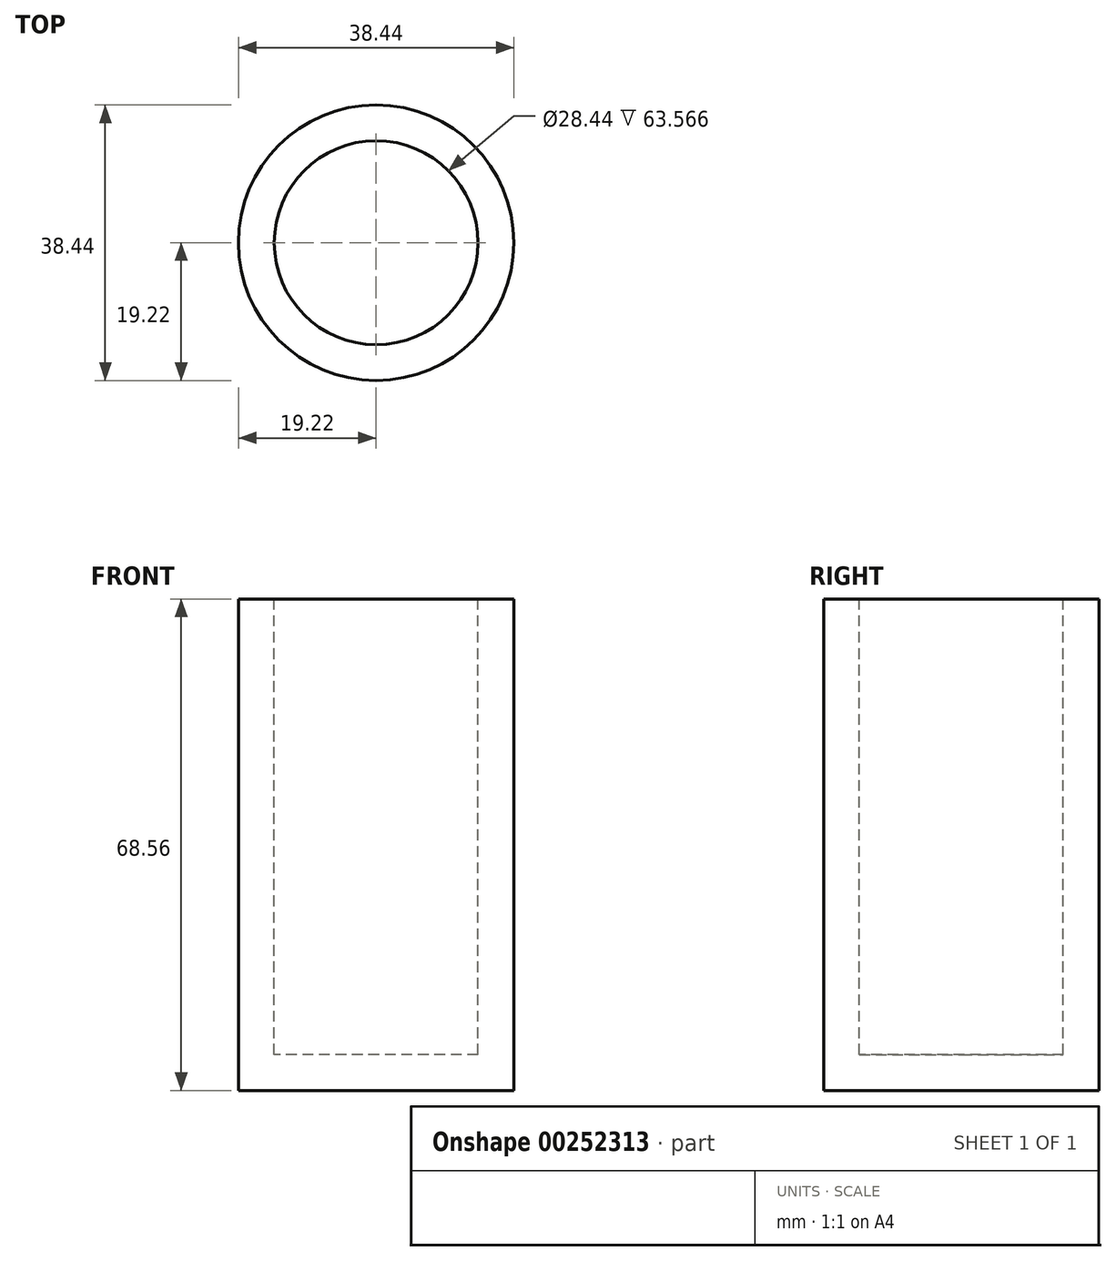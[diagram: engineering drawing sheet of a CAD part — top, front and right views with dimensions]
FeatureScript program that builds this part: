
annotation { "Feature Type Name" : "Feature", "Feature Type Description" : "" }
export const myFeature = defineFeature(function(context is Context, id is Id, definition is map)
    precondition{}
    {
        {
            var Q0;
            Q0=qCreatedBy(makeId("Front.planeOp"),FACE);
            var sketch = newSketch(context, id + "F0", { "sketchPlane" : qUnion([Q0])});
            skLineSegment(sketch, "E0.bottom", {"start": v(19.22, 34.28) * mm, "end": v(-19.22, 34.28) * mm});
            skLineSegment(sketch, "E0.top", {"start": v(19.22, -34.28) * mm, "end": v(-19.22, -34.28) * mm});
            skLineSegment(sketch, "E0.left", {"start": v(19.22, 34.28) * mm, "end": v(19.22, -34.28) * mm});
            skLineSegment(sketch, "E0.right", {"start": v(-19.22, 34.28) * mm, "end": v(-19.22, -34.28) * mm});
            skPoint(sketch, "E0.middle", {"position": v(0, 0) * mm});
            skLineSegment(sketch, "E1", {"start": v(0, 34.28) * mm, "end": v(0, -42.03) * mm});
            skPoint(sketch, "E1.endSnap0", {"position": v(0, -34.28) * mm});
            skSolve(sketch);
        }
        {
            var Q0;
            {var subQ0=sQuery(id+"F0.wireOp",EDGE,"E0.right");Q0=makeQuery(id+"F0.imprint","IMPRINT",FACE,{"disambiguationData":[TD([[makeQuery(id+"F0.imprint","IMPRINT",EDGE,{"derivedFrom":subQ0}),1.0]])]});}
            var Q1;
            Q1=sQuery(id+"F0.wireOp",EDGE,"E1");
            revolve(context, id + "F1", {"entities" : qUnion([Q0]), "axis" : qUnion([Q1]), "revolveType" : RevolveType.FULL});
        }
        {
            var Q0;
            Q0=makeQuery(id+"F1.opRevolve","SWEPT_FACE",FACE,{"disambiguationData":[OSD([sQuery(id+"F0.wireOp",EDGE,"E0.bottom")])]});
            shell(context, id + "F2", {"entities" : qUnion([Q0]), "thickness" : 5 * mm});
        }
    });
